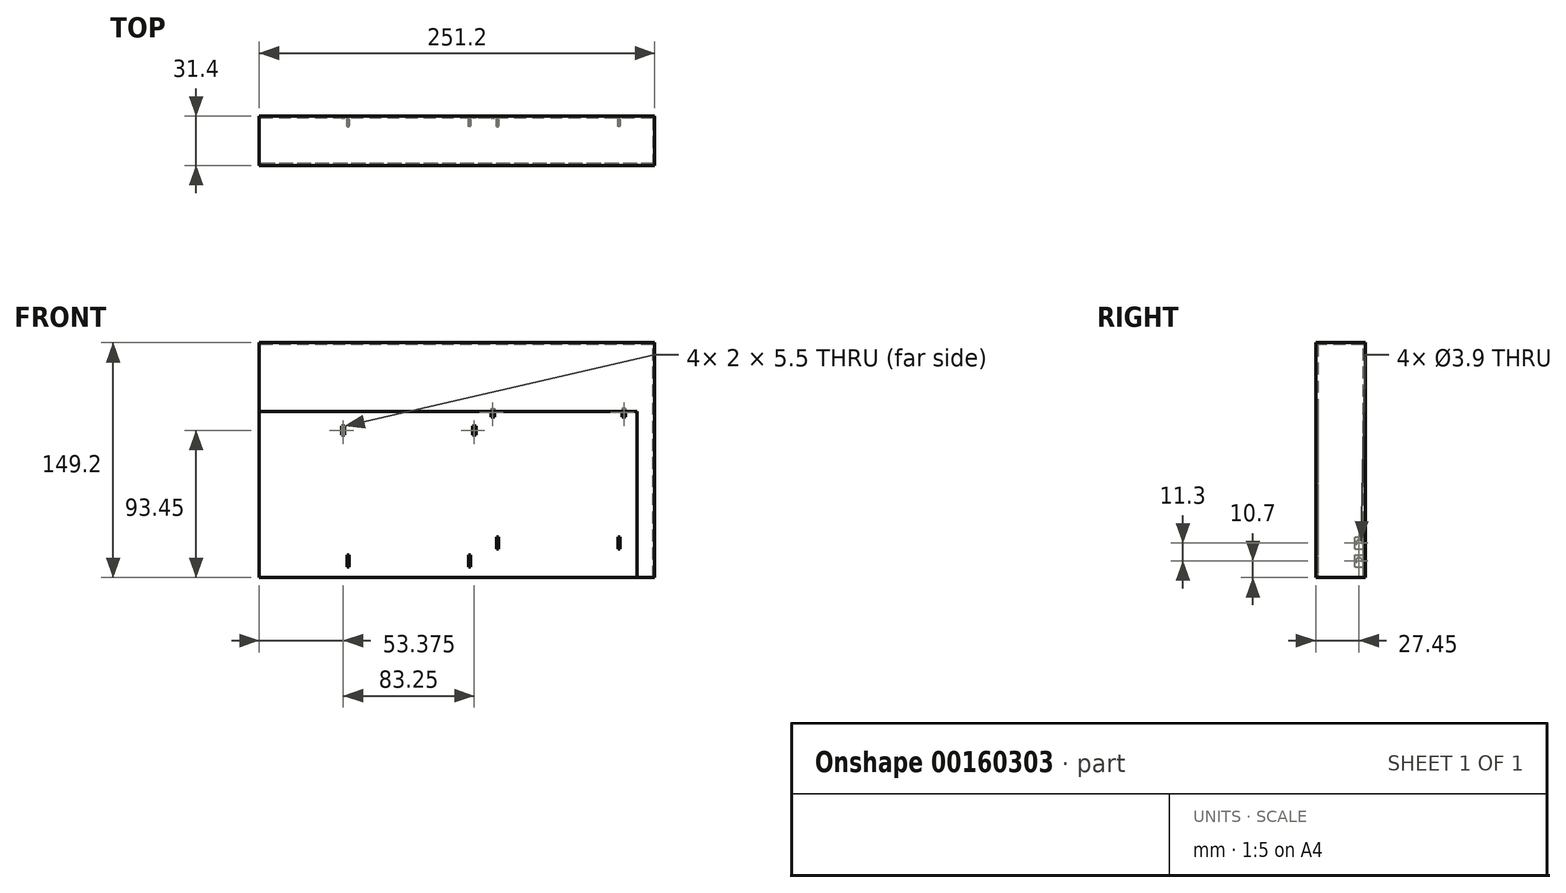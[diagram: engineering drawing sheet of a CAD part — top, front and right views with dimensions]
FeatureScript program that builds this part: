
annotation { "Feature Type Name" : "Feature", "Feature Type Description" : "" }
export const myFeature = defineFeature(function(context is Context, id is Id, definition is map)
    precondition{}
    {
        {
            var Q0;
            Q0=qCreatedBy(makeId("Right.planeOp"),FACE);
            var sketch = newSketch(context, id + "F0", { "sketchPlane" : qUnion([Q0])});
            skLineSegment(sketch, "E0", {"start": v(0, 0) * mm, "end": v(0, 148) * mm});
            skLineSegment(sketch, "E1", {"start": v(0, 148) * mm, "end": v(-29, 148) * mm});
            skLineSegment(sketch, "E2", {"start": v(-29, 148) * mm, "end": v(-29, 105.6) * mm});
            skLineSegment(sketch, "E3.0", {"start": v(-30.2, 149.2) * mm, "end": v(-30.2, 105.6) * mm});
            skLineSegment(sketch, "E3.1", {"start": v(1.2, 149.2) * mm, "end": v(-30.2, 149.2) * mm});
            skLineSegment(sketch, "E3.2", {"start": v(1.2, 0) * mm, "end": v(1.2, 149.2) * mm});
            skLineSegment(sketch, "E4", {"start": v(-29, 105.6) * mm, "end": v(-30.2, 105.6) * mm});
            skLineSegment(sketch, "E5", {"start": v(0, 0) * mm, "end": v(1.2, 0) * mm});
            skSolve(sketch);
        }
        {
            var Q0;
            Q0 = qSketchRegion(id + "F0", true);
            extrude(context, id + "F1", {"entities" : qUnion([Q0]), "endBound" : BoundingType.SYMMETRIC, "depth" : 250 * mm});
        }
        {
            var Q0;
            Q0=makeQuery(id+"F1.opExtrude","SWEPT_FACE",FACE,{"disambiguationData":[OSD([sQuery(id+"F0.wireOp",EDGE,"E5")])]});
            var sketch = newSketch(context, id + "F2", { "sketchPlane" : qUnion([Q0])});
            skLineSegment(sketch, "E6.0", {"start": v(125, 29) * mm, "end": v(-125, 29) * mm, "construction": true});
            skLineSegment(sketch, "E7", {"start": v(125, -1.2) * mm, "end": v(125, 29) * mm});
            skLineSegment(sketch, "E8", {"start": v(125, 29) * mm, "end": v(115, 29) * mm});
            skLineSegment(sketch, "E9.0", {"start": v(126.2, 30.2) * mm, "end": v(115, 30.2) * mm});
            skLineSegment(sketch, "E9.1", {"start": v(126.2, -1.2) * mm, "end": v(126.2, 30.2) * mm});
            skLineSegment(sketch, "E10", {"start": v(115, 29) * mm, "end": v(115, 30.2) * mm});
            skLineSegment(sketch, "E11", {"start": v(125, -1.2) * mm, "end": v(126.2, -1.2) * mm});
            skSolve(sketch);
        }
        {
            var Q0;
            Q0 = qSketchRegion(id + "F2", true);
            var Q1;
            Q1=makeQuery(id+"F1.opExtrude","SWEPT_FACE",FACE,{"disambiguationData":[OSD([sQuery(id+"F0.wireOp",EDGE,"E3.1")])]});
            extrude(context, id + "F3", {"entities" : qUnion([Q0]), "operationType" : NewBodyOperationType.ADD, "endBound" : BoundingType.UP_TO_SURFACE, "oppositeDirection" : true, "endBoundEntityFace" : qUnion([Q1]), "depth" : 25 * mm});
        }
        {
            var Q0;
            Q0=makeQuery(id+"F1.opExtrude","SWEPT_FACE",FACE,{"disambiguationData":[OSD([sQuery(id+"F0.wireOp",EDGE,"E0")])]});
            var sketch = newSketch(context, id + "F4", { "sketchPlane" : qUnion([Q0])});
            skLineSegment(sketch, "E12.bottom", {"start": v(104.2, 18.15) * mm, "end": v(103, 18.15) * mm});
            skLineSegment(sketch, "E12.top", {"start": v(104.2, 25.85) * mm, "end": v(103, 25.85) * mm});
            skLineSegment(sketch, "E12.left", {"start": v(104.2, 18.15) * mm, "end": v(104.2, 25.85) * mm});
            skLineSegment(sketch, "E12.right", {"start": v(103, 18.15) * mm, "end": v(103, 25.85) * mm});
            skPoint(sketch, "E12.middle", {"position": v(103.6, 22) * mm});
            skLineSegment(sketch, "E13.bottom", {"start": v(107.62, 107.5) * mm, "end": v(105.62, 107.5) * mm});
            skLineSegment(sketch, "E13.top", {"start": v(107.62, 102) * mm, "end": v(105.62, 102) * mm});
            skLineSegment(sketch, "E13.left", {"start": v(107.62, 107.5) * mm, "end": v(107.62, 102) * mm});
            skLineSegment(sketch, "E13.right", {"start": v(105.62, 107.5) * mm, "end": v(105.62, 102) * mm});
            skLineSegment(sketch, "E14", {"start": v(65, 0) * mm, "end": v(65, 148) * mm, "construction": true});
            skLineSegment(sketch, "E15", {"start": v(-30, 0) * mm, "end": v(-30, 148) * mm, "construction": true});
            skLineSegment(sketch, "E16.MirrorCS", {"start": v(22.37, 107.5) * mm, "end": v(22.37, 102) * mm});
            skLineSegment(sketch, "E17.MirrorCS", {"start": v(22.38, 107.5) * mm, "end": v(24.38, 107.5) * mm});
            skLineSegment(sketch, "E18.MirrorCS", {"start": v(24.38, 107.5) * mm, "end": v(24.38, 102) * mm});
            skLineSegment(sketch, "E19.MirrorCS", {"start": v(22.38, 102) * mm, "end": v(24.38, 102) * mm});
            skLineSegment(sketch, "E20.MirrorCS", {"start": v(25.8, 18.15) * mm, "end": v(25.8, 25.85) * mm});
            skLineSegment(sketch, "E21.MirrorCS", {"start": v(25.8, 25.85) * mm, "end": v(27, 25.85) * mm});
            skLineSegment(sketch, "E22.MirrorCS", {"start": v(27, 18.15) * mm, "end": v(27, 25.85) * mm});
            skLineSegment(sketch, "E23.MirrorCS", {"start": v(25.8, 18.15) * mm, "end": v(27, 18.15) * mm});
            skLineSegment(sketch, "E24.1.0.0", {"start": v(-70.63, 96.2) * mm, "end": v(-70.63, 90.7) * mm});
            skLineSegment(sketch, "E24.1.0.1", {"start": v(-72.62, 96.2) * mm, "end": v(-70.62, 96.2) * mm});
            skLineSegment(sketch, "E24.1.0.2", {"start": v(-72.63, 96.2) * mm, "end": v(-72.63, 90.7) * mm});
            skLineSegment(sketch, "E24.1.0.3", {"start": v(-72.62, 90.7) * mm, "end": v(-70.62, 90.7) * mm});
            skLineSegment(sketch, "E24.1.0.4", {"start": v(-69.2, 6.85) * mm, "end": v(-69.2, 14.55) * mm});
            skLineSegment(sketch, "E24.1.0.5", {"start": v(-68, 6.85) * mm, "end": v(-68, 14.55) * mm});
            skLineSegment(sketch, "E24.1.0.6", {"start": v(-69.2, 6.85) * mm, "end": v(-68, 6.85) * mm});
            skLineSegment(sketch, "E24.1.0.7", {"start": v(-69.2, 14.55) * mm, "end": v(-68, 14.55) * mm});
            skLineSegment(sketch, "E24.1.0.8", {"start": v(8, 6.85) * mm, "end": v(8, 14.55) * mm});
            skLineSegment(sketch, "E24.1.0.9", {"start": v(9.2, 6.85) * mm, "end": v(9.2, 14.55) * mm});
            skPoint(sketch, "E24.1.0.10", {"position": v(8.6, 10.7) * mm});
            skLineSegment(sketch, "E24.1.0.11", {"start": v(9.2, 14.55) * mm, "end": v(8, 14.55) * mm});
            skLineSegment(sketch, "E24.1.0.12", {"start": v(9.2, 6.85) * mm, "end": v(8, 6.85) * mm});
            skLineSegment(sketch, "E24.1.0.13", {"start": v(12.62, 96.2) * mm, "end": v(10.62, 96.2) * mm});
            skLineSegment(sketch, "E24.1.0.14", {"start": v(10.62, 96.2) * mm, "end": v(10.62, 90.7) * mm});
            skLineSegment(sketch, "E24.1.0.15", {"start": v(12.62, 90.7) * mm, "end": v(10.62, 90.7) * mm});
            skLineSegment(sketch, "E24.1.0.16", {"start": v(12.62, 96.2) * mm, "end": v(12.62, 90.7) * mm});
            skLineSegment(sketch, "E24.direction1", {"start": v(24.38, 102) * mm, "end": v(-70.62, 90.7) * mm, "construction": true});
            skSolve(sketch);
        }
        {
            var Q0;
            Q0=makeQuery(id+"F4.imprint","IMPRINT",FACE,{"disambiguationData":[TD([[makeQuery(id+"F4.imprint","IMPRINT",EDGE,{"derivedFrom":sQuery(id+"F4.wireOp",EDGE,"E16.MirrorCS")}),1.0]])]});
            var Q1;
            Q1=makeQuery(id+"F4.imprint","IMPRINT",FACE,{"disambiguationData":[TD([[makeQuery(id+"F4.imprint","IMPRINT",EDGE,{"derivedFrom":sQuery(id+"F4.wireOp",EDGE,"E13.bottom")}),1.0]])]});
            var Q2;
            Q2=makeQuery(id+"F4.imprint","IMPRINT",FACE,{"disambiguationData":[TD([[makeQuery(id+"F4.imprint","IMPRINT",EDGE,{"derivedFrom":sQuery(id+"F4.wireOp",EDGE,"E24.1.0.13")}),1.0]])]});
            var Q3;
            Q3=makeQuery(id+"F4.imprint","IMPRINT",FACE,{"disambiguationData":[TD([[makeQuery(id+"F4.imprint","IMPRINT",EDGE,{"derivedFrom":sQuery(id+"F4.wireOp",EDGE,"E24.1.0.0")}),-1.0]])]});
            extrude(context, id + "F5", {"entities" : qUnion([Q0, Q1, Q2, Q3]), "operationType" : NewBodyOperationType.REMOVE, "endBound" : BoundingType.THROUGH_ALL, "oppositeDirection" : true, "depth" : 25 * mm});
        }
        {
            var Q0;
            Q0=makeQuery(id+"F4.imprint","IMPRINT",FACE,{"disambiguationData":[TD([[makeQuery(id+"F4.imprint","IMPRINT",EDGE,{"derivedFrom":sQuery(id+"F4.wireOp",EDGE,"E20.MirrorCS")}),-1.0]])]});
            var Q1;
            Q1=makeQuery(id+"F4.imprint","IMPRINT",FACE,{"disambiguationData":[TD([[makeQuery(id+"F4.imprint","IMPRINT",EDGE,{"derivedFrom":sQuery(id+"F4.wireOp",EDGE,"E12.bottom")}),-1.0]])]});
            var Q2;
            Q2=makeQuery(id+"F4.imprint","IMPRINT",FACE,{"disambiguationData":[TD([[makeQuery(id+"F4.imprint","IMPRINT",EDGE,{"derivedFrom":sQuery(id+"F4.wireOp",EDGE,"E24.1.0.4")}),-1.0]])]});
            var Q3;
            Q3=makeQuery(id+"F4.imprint","IMPRINT",FACE,{"disambiguationData":[TD([[makeQuery(id+"F4.imprint","IMPRINT",EDGE,{"derivedFrom":sQuery(id+"F4.wireOp",EDGE,"E24.1.0.8")}),-1.0]])]});
            extrude(context, id + "F6", {"entities" : qUnion([Q0, Q1, Q2, Q3]), "operationType" : NewBodyOperationType.ADD, "depth" : 5.5 * mm});
        }
        {
            var Q0;
            Q0=makeQuery(id+"F6.opExtrude","SWEPT_FACE",FACE,{"disambiguationData":[OSD([sQuery(id+"F4.wireOp",EDGE,"E20.MirrorCS")])]});
            var sketch = newSketch(context, id + "F7", { "sketchPlane" : qUnion([Q0])});
            skCircle(sketch, "E25", {"center": v(2.75, 22) * mm, "radius": 1.95 * mm});
            skPoint(sketch, "E25.centerSnap0", {"position": v(5.5, 22) * mm});
            skPoint(sketch, "E25.centerSnap1", {"position": v(2.75, 25.85) * mm});
            skSolve(sketch);
        }
        {
            var Q0;
            Q0=makeQuery(id+"F6.opExtrude","SWEPT_FACE",FACE,{"disambiguationData":[OSD([sQuery(id+"F4.wireOp",EDGE,"E24.1.0.4")])]});
            var sketch = newSketch(context, id + "F8", { "sketchPlane" : qUnion([Q0])});
            skCircle(sketch, "E26", {"center": v(2.75, 10.7) * mm, "radius": 1.95 * mm});
            skPoint(sketch, "E26.centerSnap0", {"position": v(5.5, 10.7) * mm});
            skPoint(sketch, "E26.centerSnap1", {"position": v(2.75, 14.55) * mm});
            skSolve(sketch);
        }
        {
            var Q0;
            Q0=makeQuery(id+"F7.imprint","IMPRINT",FACE,{"disambiguationData":[TD([[makeQuery(id+"F7.imprint","IMPRINT",EDGE,{"derivedFrom":sQuery(id+"F7.wireOp",EDGE,"E25")}),1.0]])]});
            var Q1;
            Q1=makeQuery(id+"F8.imprint","IMPRINT",FACE,{"disambiguationData":[TD([[makeQuery(id+"F8.imprint","IMPRINT",EDGE,{"derivedFrom":sQuery(id+"F8.wireOp",EDGE,"E26")}),1.0]])]});
            var Q2;
            Q2=makeQuery(id+"F6.opExtrude","SWEPT_FACE",FACE,{"disambiguationData":[OSD([sQuery(id+"F4.wireOp",EDGE,"E12.left")])]});
            extrude(context, id + "F9", {"entities" : qUnion([Q0, Q1]), "operationType" : NewBodyOperationType.REMOVE, "endBound" : BoundingType.UP_TO_SURFACE, "oppositeDirection" : true, "endBoundEntityFace" : qUnion([Q2]), "depth" : 25 * mm});
        }
    });
